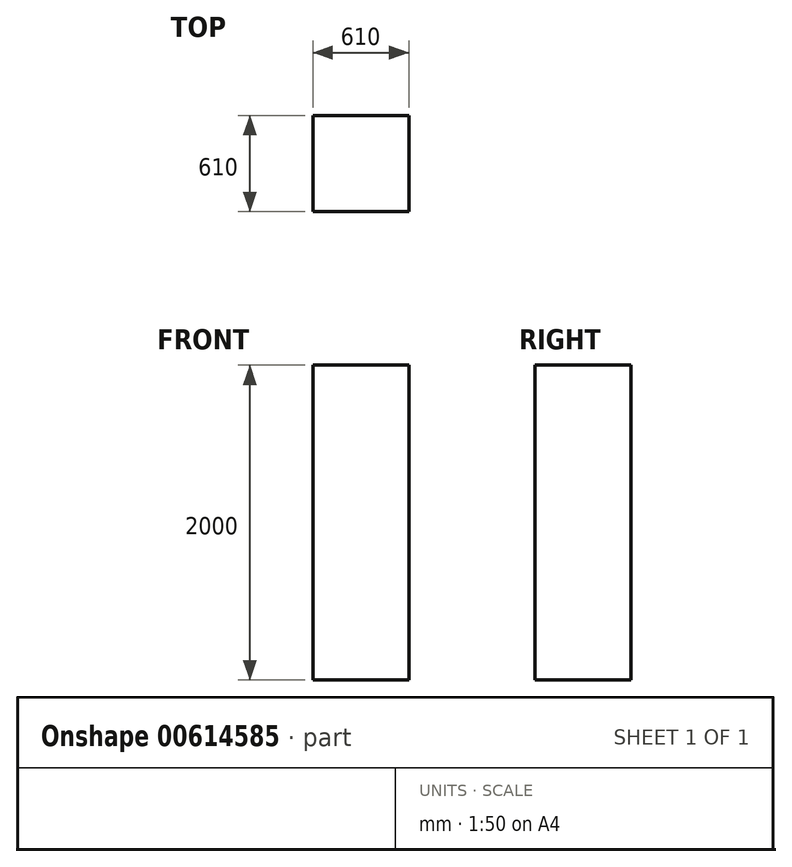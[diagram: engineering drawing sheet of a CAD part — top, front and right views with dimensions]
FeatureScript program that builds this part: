
annotation { "Feature Type Name" : "Feature", "Feature Type Description" : "" }
export const myFeature = defineFeature(function(context is Context, id is Id, definition is map)
    precondition{}
    {
        {
            var Q0;
            Q0=qCreatedBy(makeId("Top.planeOp"),FACE);
            var sketch = newSketch(context, id + "F0", { "sketchPlane" : qUnion([Q0])});
            skLineSegment(sketch, "E0.bottom", {"start": v(0, 0) * mm, "end": v(610, 0) * mm});
            skLineSegment(sketch, "E0.top", {"start": v(0, -610) * mm, "end": v(610, -610) * mm});
            skLineSegment(sketch, "E0.left", {"start": v(0, 0) * mm, "end": v(0, -610) * mm});
            skLineSegment(sketch, "E0.right", {"start": v(610, 0) * mm, "end": v(610, -610) * mm});
            skSolve(sketch);
        }
        {
            var Q0;
            Q0=makeQuery(id+"F0.imprint","IMPRINT",FACE,{"disambiguationData":[TD([[makeQuery(id+"F0.imprint","IMPRINT",EDGE,{"derivedFrom":sQuery(id+"F0.wireOp",EDGE,"E0.bottom")}),-1.0]])]});
            extrude(context, id + "F1", {"entities" : qUnion([Q0]), "depth" : 2000 * mm, "offsetDistance" : 25 * mm});
        }
        {
            var Q0;
            Q0=makeQuery(id+"F1.opExtrude","CAP_EDGE",EDGE,{"disambiguationData":[OSD([sQuery(id+"F0.wireOp",EDGE,"E0.left")])],"isStart":false});
            cPoint(context, id + "F2", {"entities" : qUnion([Q0]), "parameter" : 0.5});
        }
        {
            var Q0;
            Q0=makeQuery(id+"F1.opExtrude","CAP_EDGE",EDGE,{"disambiguationData":[OSD([sQuery(id+"F0.wireOp",EDGE,"E0.right")])],"isStart":false});
            cPoint(context, id + "F3", {"entities" : qUnion([Q0]), "parameter" : 0.5});
        }
        {
            var Q0;
            Q0=makeQuery(id+"F1.opExtrude","CAP_EDGE",EDGE,{"disambiguationData":[OSD([sQuery(id+"F0.wireOp",EDGE,"E0.right")])],"isStart":true});
            cPoint(context, id + "F4", {"entities" : qUnion([Q0]), "parameter" : 0.5});
        }
        {
            var Q0;
            Q0=qCreatedBy(id+"F2",VERTEX);
            var Q1;
            Q1=qCreatedBy(id+"F3",VERTEX);
            var Q2;
            Q2=qCreatedBy(id+"F4",VERTEX);
            cPlane(context, id + "F5", {"entities" : qUnion([Q0, Q1, Q2]), "cplaneType" : CPlaneType.THREE_POINT, "offset" : 25 * mm, "width" : 150 * mm, "height" : 150 * mm});
        }
        {
            var Q0;
            Q0=makeQuery(id+"F1.opExtrude","SWEPT_BODY",BODY,{"disambiguationData":[OSD([sQuery(id+"F0.wireOp",EDGE,"E0.bottom"),sQuery(id+"F0.wireOp",EDGE,"E0.top"),sQuery(id+"F0.wireOp",EDGE,"E0.left"),sQuery(id+"F0.wireOp",EDGE,"E0.right")])]});
            var Q1;
            Q1=qCreatedBy(id+"F5.planeOp",FACE);
            mirror(context, id + "F6", {"operationType" : NewBodyOperationType.ADD, "entities" : qUnion([Q0]), "mirrorPlane" : qUnion([Q1])});
        }
    });
